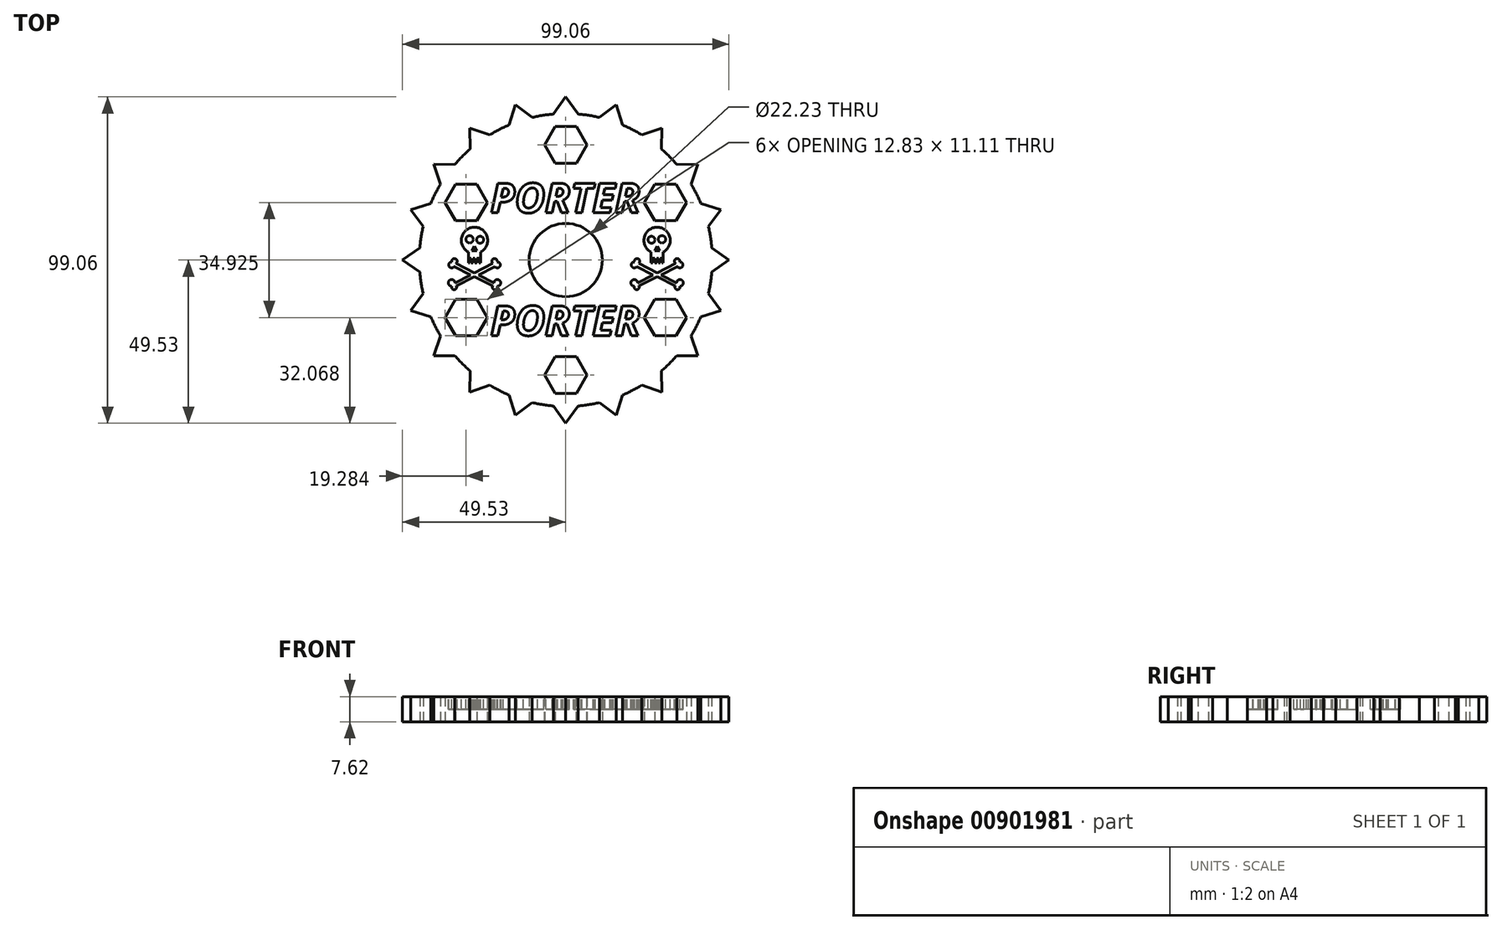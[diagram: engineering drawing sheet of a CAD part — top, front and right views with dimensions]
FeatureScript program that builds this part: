
annotation { "Feature Type Name" : "Feature", "Feature Type Description" : "" }
export const myFeature = defineFeature(function(context is Context, id is Id, definition is map)
    precondition{}
    {
        {
            var Q0;
            Q0=qCreatedBy(makeId("Top.planeOp"),FACE);
            var sketch = newSketch(context, id + "F0", { "sketchPlane" : qUnion([Q0])});
            skCircle(sketch, "E0", {"center": v(0, 0) * mm, "radius": 11.11 * mm});
            skCircle(sketch, "E1", {"center": v(0, 0) * mm, "radius": 44.45 * mm});
            skCircle(sketch, "E2.cCircle", {"center": v(0, 34.93) * mm, "radius": 5.56 * mm, "construction": true});
            skLineSegment(sketch, "E2.0", {"start": v(6.42, 34.92) * mm, "end": v(3.2, 29.37) * mm});
            skLineSegment(sketch, "E2.1", {"start": v(3.2, 29.37) * mm, "end": v(-3.2, 29.37) * mm});
            skLineSegment(sketch, "E2.2", {"start": v(-3.2, 29.37) * mm, "end": v(-6.42, 34.93) * mm});
            skLineSegment(sketch, "E2.3", {"start": v(-6.42, 34.93) * mm, "end": v(-3.2, 40.48) * mm});
            skLineSegment(sketch, "E2.4", {"start": v(-3.2, 40.48) * mm, "end": v(3.2, 40.48) * mm});
            skLineSegment(sketch, "E2.5", {"start": v(3.2, 40.48) * mm, "end": v(6.42, 34.92) * mm});
            skPoint(sketch, "E2.0.midPoint", {"position": v(4.81, 32.15) * mm});
            skCircle(sketch, "E3.1.0", {"center": v(-30.25, 17.46) * mm, "radius": 5.56 * mm, "construction": true});
            skCircle(sketch, "E3.2.0", {"center": v(-30.25, -17.46) * mm, "radius": 5.56 * mm, "construction": true});
            skCircle(sketch, "E3.3.0", {"center": v(0, -34.93) * mm, "radius": 5.56 * mm, "construction": true});
            skCircle(sketch, "E3.4.0", {"center": v(30.25, -17.46) * mm, "radius": 5.56 * mm, "construction": true});
            skCircle(sketch, "E3.5.0", {"center": v(30.25, 17.46) * mm, "radius": 5.56 * mm, "construction": true});
            skSolve(sketch);
        }
        {
            var Q0;
            Q0 = qSketchRegion(id + "F0", true);
            extrude(context, id + "F1", {"entities" : qUnion([Q0]), "depth" : 7.62 * mm, "offsetDistance" : 25.4 * mm});
        }
        {
            var Q0;
            Q0=makeQuery(id+"F1.opExtrude","CAP_FACE",FACE,{"disambiguationData":[OSD([sQuery(id+"F0.wireOp",EDGE,"E0"),sQuery(id+"F0.wireOp",EDGE,"E1"),sQuery(id+"F0.wireOp",EDGE,"E2.0"),sQuery(id+"F0.wireOp",EDGE,"E2.1"),sQuery(id+"F0.wireOp",EDGE,"E2.2"),sQuery(id+"F0.wireOp",EDGE,"E2.3"),sQuery(id+"F0.wireOp",EDGE,"E2.4"),sQuery(id+"F0.wireOp",EDGE,"E2.5")])],"isStart":true});
            var sketch = newSketch(context, id + "F2", { "sketchPlane" : qUnion([Q0])});
            skLineSegment(sketch, "E4", {"start": v(0, 0) * mm, "end": v(0, -34.93) * mm});
            skCircle(sketch, "E5.cCircle", {"center": v(0, -34.93) * mm, "radius": 5.56 * mm, "construction": true});
            skPoint(sketch, "E5.cCircle.perimeterSnap0", {"position": v(0, -40.48) * mm});
            skLineSegment(sketch, "E5.0", {"start": v(-3.2, -29.37) * mm, "end": v(3.2, -29.37) * mm});
            skLineSegment(sketch, "E5.1", {"start": v(3.2, -29.37) * mm, "end": v(6.42, -34.93) * mm});
            skLineSegment(sketch, "E5.2", {"start": v(6.42, -34.93) * mm, "end": v(3.2, -40.48) * mm});
            skLineSegment(sketch, "E5.3", {"start": v(3.2, -40.48) * mm, "end": v(-3.2, -40.48) * mm});
            skLineSegment(sketch, "E5.4", {"start": v(-3.2, -40.48) * mm, "end": v(-6.42, -34.92) * mm});
            skLineSegment(sketch, "E5.5", {"start": v(-6.42, -34.92) * mm, "end": v(-3.2, -29.37) * mm});
            skPoint(sketch, "E5.0.midPoint", {"position": v(0, -29.37) * mm});
            skPoint(sketch, "E5.0.midPoint.positionSnap0", {"position": v(0, -40.48) * mm});
            skCircle(sketch, "E6.1.0", {"center": v(30.25, -17.46) * mm, "radius": 5.56 * mm, "construction": true});
            skPoint(sketch, "E6.1.1", {"position": v(25.44, -14.68) * mm});
            skPoint(sketch, "E6.1.2", {"position": v(35.06, -20.24) * mm});
            skLineSegment(sketch, "E6.1.3", {"start": v(33.45, -23.02) * mm, "end": v(27.04, -23.02) * mm});
            skLineSegment(sketch, "E6.1.4", {"start": v(23.83, -17.46) * mm, "end": v(27.04, -11.9) * mm});
            skPoint(sketch, "E6.1.5", {"position": v(35.06, -20.24) * mm});
            skLineSegment(sketch, "E6.1.6", {"start": v(33.45, -11.9) * mm, "end": v(36.66, -17.46) * mm});
            skLineSegment(sketch, "E6.1.7", {"start": v(27.04, -23.02) * mm, "end": v(23.83, -17.46) * mm});
            skLineSegment(sketch, "E6.1.8", {"start": v(27.04, -11.9) * mm, "end": v(33.45, -11.9) * mm});
            skLineSegment(sketch, "E6.1.9", {"start": v(36.66, -17.46) * mm, "end": v(33.45, -23.02) * mm});
            skCircle(sketch, "E6.2.0", {"center": v(30.25, 17.46) * mm, "radius": 5.56 * mm, "construction": true});
            skPoint(sketch, "E6.2.1", {"position": v(25.43, 14.69) * mm});
            skPoint(sketch, "E6.2.2", {"position": v(35.06, 20.24) * mm});
            skLineSegment(sketch, "E6.2.3", {"start": v(36.66, 17.46) * mm, "end": v(33.45, 11.9) * mm});
            skLineSegment(sketch, "E6.2.4", {"start": v(27.04, 11.9) * mm, "end": v(23.83, 17.46) * mm});
            skPoint(sketch, "E6.2.5", {"position": v(35.06, 20.24) * mm});
            skLineSegment(sketch, "E6.2.6", {"start": v(27.04, 23.02) * mm, "end": v(33.45, 23.02) * mm});
            skLineSegment(sketch, "E6.2.7", {"start": v(33.45, 11.9) * mm, "end": v(27.04, 11.9) * mm});
            skLineSegment(sketch, "E6.2.8", {"start": v(23.83, 17.46) * mm, "end": v(27.04, 23.02) * mm});
            skLineSegment(sketch, "E6.2.9", {"start": v(33.45, 23.02) * mm, "end": v(36.66, 17.46) * mm});
            skCircle(sketch, "E6.3.0", {"center": v(0, 34.93) * mm, "radius": 5.56 * mm, "construction": true});
            skPoint(sketch, "E6.3.1", {"position": v(0, 29.37) * mm});
            skPoint(sketch, "E6.3.2", {"position": v(0, 40.48) * mm});
            skLineSegment(sketch, "E6.3.3", {"start": v(3.2, 40.48) * mm, "end": v(6.42, 34.92) * mm});
            skLineSegment(sketch, "E6.3.4", {"start": v(3.2, 29.37) * mm, "end": v(-3.2, 29.37) * mm});
            skPoint(sketch, "E6.3.5", {"position": v(0, 40.48) * mm});
            skLineSegment(sketch, "E6.3.6", {"start": v(-6.42, 34.93) * mm, "end": v(-3.2, 40.48) * mm});
            skLineSegment(sketch, "E6.3.7", {"start": v(6.42, 34.92) * mm, "end": v(3.2, 29.37) * mm});
            skLineSegment(sketch, "E6.3.8", {"start": v(-3.2, 29.37) * mm, "end": v(-6.42, 34.93) * mm});
            skLineSegment(sketch, "E6.3.9", {"start": v(-3.2, 40.48) * mm, "end": v(3.2, 40.48) * mm});
            skCircle(sketch, "E6.4.0", {"center": v(-30.25, 17.46) * mm, "radius": 5.56 * mm, "construction": true});
            skPoint(sketch, "E6.4.1", {"position": v(-25.44, 14.68) * mm});
            skPoint(sketch, "E6.4.2", {"position": v(-35.06, 20.24) * mm});
            skLineSegment(sketch, "E6.4.3", {"start": v(-33.45, 23.02) * mm, "end": v(-27.04, 23.02) * mm});
            skLineSegment(sketch, "E6.4.4", {"start": v(-23.83, 17.46) * mm, "end": v(-27.04, 11.9) * mm});
            skPoint(sketch, "E6.4.5", {"position": v(-35.06, 20.24) * mm});
            skLineSegment(sketch, "E6.4.6", {"start": v(-33.45, 11.9) * mm, "end": v(-36.66, 17.46) * mm});
            skLineSegment(sketch, "E6.4.7", {"start": v(-27.04, 23.02) * mm, "end": v(-23.83, 17.46) * mm});
            skLineSegment(sketch, "E6.4.8", {"start": v(-27.04, 11.9) * mm, "end": v(-33.45, 11.9) * mm});
            skLineSegment(sketch, "E6.4.9", {"start": v(-36.66, 17.46) * mm, "end": v(-33.45, 23.02) * mm});
            skCircle(sketch, "E6.5.0", {"center": v(-30.25, -17.46) * mm, "radius": 5.56 * mm, "construction": true});
            skPoint(sketch, "E6.5.1", {"position": v(-25.43, -14.69) * mm});
            skPoint(sketch, "E6.5.2", {"position": v(-35.06, -20.24) * mm});
            skLineSegment(sketch, "E6.5.3", {"start": v(-36.66, -17.46) * mm, "end": v(-33.45, -11.9) * mm});
            skLineSegment(sketch, "E6.5.4", {"start": v(-27.04, -11.9) * mm, "end": v(-23.83, -17.46) * mm});
            skPoint(sketch, "E6.5.5", {"position": v(-35.06, -20.24) * mm});
            skLineSegment(sketch, "E6.5.6", {"start": v(-27.04, -23.02) * mm, "end": v(-33.45, -23.02) * mm});
            skLineSegment(sketch, "E6.5.7", {"start": v(-33.45, -11.9) * mm, "end": v(-27.04, -11.9) * mm});
            skLineSegment(sketch, "E6.5.8", {"start": v(-23.83, -17.46) * mm, "end": v(-27.04, -23.02) * mm});
            skLineSegment(sketch, "E6.5.9", {"start": v(-33.45, -23.02) * mm, "end": v(-36.66, -17.46) * mm});
            skPoint(sketch, "E6.center", {"position": v(0, 0) * mm});
            skSolve(sketch);
        }
        {
            var Q0;
            Q0 = qSketchRegion(id + "F2", true);
            extrude(context, id + "F3", {"entities" : qUnion([Q0]), "operationType" : NewBodyOperationType.REMOVE, "oppositeDirection" : true, "depth" : 25.4 * mm, "offsetDistance" : 25.4 * mm});
        }
        {
            var Q0;
            Q0=makeQuery(id+"F1.opExtrude","CAP_FACE",FACE,{"disambiguationData":[OSD([sQuery(id+"F0.wireOp",EDGE,"E0"),sQuery(id+"F0.wireOp",EDGE,"E1"),sQuery(id+"F0.wireOp",EDGE,"E2.0"),sQuery(id+"F0.wireOp",EDGE,"E2.1"),sQuery(id+"F0.wireOp",EDGE,"E2.2"),sQuery(id+"F0.wireOp",EDGE,"E2.3"),sQuery(id+"F0.wireOp",EDGE,"E2.4"),sQuery(id+"F0.wireOp",EDGE,"E2.5")])],"isStart":false});
            var sketch = newSketch(context, id + "F4", { "sketchPlane" : qUnion([Q0])});
            skText(sketch, "E7", { "text": "PORTER", "fontName": "OpenSans-BoldItalic.ttf"});
            skText(sketch, "E8", { "text": "PORTER", "fontName": "OpenSans-BoldItalic.ttf"});
            const initialGuessF4  = {"E7": [-0.0228, -0.02292, 1, 0, 0.00907], "E8": [-0.0228, 0.01432, 1, 0, 0.00907]};
            skSetInitialGuess(sketch, initialGuessF4);
            skSolve(sketch);
        }
        {
            var Q0;
            Q0 = qSketchRegion(id + "F4", true);
            extrude(context, id + "F5", {"entities" : qUnion([Q0]), "operationType" : NewBodyOperationType.REMOVE, "oppositeDirection" : true, "depth" : 3.8 * mm, "offsetDistance" : 25.4 * mm});
        }
        {
            var Q0;
            {var subQ0=sQuery(id+"F0.wireOp",EDGE,"E2.5");var subQ1=sQuery(id+"F0.wireOp",EDGE,"E2.4");var subQ2=sQuery(id+"F0.wireOp",EDGE,"E2.0");var subQ3=sQuery(id+"F0.wireOp",EDGE,"E1");var subQ4=sQuery(id+"F0.wireOp",EDGE,"E2.1");var subQ5=sQuery(id+"F0.wireOp",EDGE,"E2.2");var subQ6=sQuery(id+"F0.wireOp",EDGE,"E0");var subQ7=sQuery(id+"F0.wireOp",EDGE,"E2.3");Q0=makeQuery(id+"F5.boolean.opBoolean","SPLIT",FACE,{"disambiguationData":[TD([makeQuery(id+"F1.opExtrude","SWEPT_FACE",FACE,{"disambiguationData":[OSD([subQ6])]})])],"derivedFrom":makeQuery(id+"F1.opExtrude","CAP_FACE",FACE,{"disambiguationData":[OSD([subQ6,subQ3,subQ2,subQ4,subQ5,subQ7,subQ1,subQ0])],"isStart":false})});}
            var sketch = newSketch(context, id + "F6", { "sketchPlane" : qUnion([Q0])});
            skLineSegment(sketch, "E9", {"start": v(0, 49.53) * mm, "end": v(4.7, 42.86) * mm});
            skLineSegment(sketch, "E10.MirrorCS", {"start": v(0, 49.53) * mm, "end": v(-4.7, 42.86) * mm});
            skLineSegment(sketch, "E11", {"start": v(-4.7, 42.86) * mm, "end": v(4.7, 42.86) * mm});
            skLineSegment(sketch, "E12.1.0", {"start": v(-15.3, 47.1) * mm, "end": v(-8.77, 42.22) * mm});
            skLineSegment(sketch, "E12.1.1", {"start": v(-17.72, 39.3) * mm, "end": v(-8.77, 42.22) * mm});
            skLineSegment(sketch, "E12.1.2", {"start": v(-15.3, 47.1) * mm, "end": v(-17.72, 39.3) * mm});
            skLineSegment(sketch, "E12.2.0", {"start": v(-29.11, 40.07) * mm, "end": v(-21.38, 37.44) * mm});
            skLineSegment(sketch, "E12.2.1", {"start": v(-29, 31.9) * mm, "end": v(-21.38, 37.44) * mm});
            skLineSegment(sketch, "E12.2.2", {"start": v(-29.11, 40.07) * mm, "end": v(-29, 31.9) * mm});
            skLineSegment(sketch, "E12.3.0", {"start": v(-40.07, 29.11) * mm, "end": v(-31.9, 29) * mm});
            skLineSegment(sketch, "E12.3.1", {"start": v(-37.44, 21.38) * mm, "end": v(-31.9, 29) * mm});
            skLineSegment(sketch, "E12.3.2", {"start": v(-40.07, 29.11) * mm, "end": v(-37.44, 21.38) * mm});
            skLineSegment(sketch, "E12.4.0", {"start": v(-47.1, 15.3) * mm, "end": v(-39.3, 17.72) * mm});
            skLineSegment(sketch, "E12.4.1", {"start": v(-42.22, 8.77) * mm, "end": v(-39.3, 17.72) * mm});
            skLineSegment(sketch, "E12.4.2", {"start": v(-47.1, 15.3) * mm, "end": v(-42.22, 8.77) * mm});
            skLineSegment(sketch, "E12.5.0", {"start": v(-49.53, 0) * mm, "end": v(-42.86, 4.7) * mm});
            skLineSegment(sketch, "E12.5.1", {"start": v(-42.86, -4.7) * mm, "end": v(-42.86, 4.7) * mm});
            skLineSegment(sketch, "E12.5.2", {"start": v(-49.53, 0) * mm, "end": v(-42.86, -4.7) * mm});
            skLineSegment(sketch, "E12.6.0", {"start": v(-47.1, -15.3) * mm, "end": v(-42.22, -8.77) * mm});
            skLineSegment(sketch, "E12.6.1", {"start": v(-39.3, -17.72) * mm, "end": v(-42.22, -8.77) * mm});
            skLineSegment(sketch, "E12.6.2", {"start": v(-47.1, -15.3) * mm, "end": v(-39.3, -17.72) * mm});
            skLineSegment(sketch, "E12.7.0", {"start": v(-40.07, -29.11) * mm, "end": v(-37.44, -21.38) * mm});
            skLineSegment(sketch, "E12.7.1", {"start": v(-31.9, -29) * mm, "end": v(-37.44, -21.38) * mm});
            skLineSegment(sketch, "E12.7.2", {"start": v(-40.07, -29.11) * mm, "end": v(-31.9, -29) * mm});
            skLineSegment(sketch, "E12.8.0", {"start": v(-29.11, -40.07) * mm, "end": v(-29, -31.9) * mm});
            skLineSegment(sketch, "E12.8.1", {"start": v(-21.38, -37.44) * mm, "end": v(-29, -31.9) * mm});
            skLineSegment(sketch, "E12.8.2", {"start": v(-29.11, -40.07) * mm, "end": v(-21.38, -37.44) * mm});
            skLineSegment(sketch, "E12.9.0", {"start": v(-15.3, -47.1) * mm, "end": v(-17.72, -39.3) * mm});
            skLineSegment(sketch, "E12.9.1", {"start": v(-8.77, -42.22) * mm, "end": v(-17.72, -39.3) * mm});
            skLineSegment(sketch, "E12.9.2", {"start": v(-15.3, -47.1) * mm, "end": v(-8.77, -42.22) * mm});
            skLineSegment(sketch, "E12.10.0", {"start": v(0, -49.53) * mm, "end": v(-4.7, -42.86) * mm});
            skLineSegment(sketch, "E12.10.1", {"start": v(4.7, -42.86) * mm, "end": v(-4.7, -42.86) * mm});
            skLineSegment(sketch, "E12.10.2", {"start": v(0, -49.53) * mm, "end": v(4.7, -42.86) * mm});
            skLineSegment(sketch, "E12.11.0", {"start": v(15.3, -47.1) * mm, "end": v(8.77, -42.22) * mm});
            skLineSegment(sketch, "E12.11.1", {"start": v(17.72, -39.3) * mm, "end": v(8.77, -42.22) * mm});
            skLineSegment(sketch, "E12.11.2", {"start": v(15.3, -47.1) * mm, "end": v(17.72, -39.3) * mm});
            skLineSegment(sketch, "E12.12.0", {"start": v(29.11, -40.07) * mm, "end": v(21.38, -37.44) * mm});
            skLineSegment(sketch, "E12.12.1", {"start": v(29, -31.9) * mm, "end": v(21.38, -37.44) * mm});
            skLineSegment(sketch, "E12.12.2", {"start": v(29.11, -40.07) * mm, "end": v(29, -31.9) * mm});
            skLineSegment(sketch, "E12.13.0", {"start": v(40.07, -29.11) * mm, "end": v(31.9, -29) * mm});
            skLineSegment(sketch, "E12.13.1", {"start": v(37.44, -21.38) * mm, "end": v(31.9, -29) * mm});
            skLineSegment(sketch, "E12.13.2", {"start": v(40.07, -29.11) * mm, "end": v(37.44, -21.38) * mm});
            skLineSegment(sketch, "E12.14.0", {"start": v(47.1, -15.3) * mm, "end": v(39.3, -17.72) * mm});
            skLineSegment(sketch, "E12.14.1", {"start": v(42.22, -8.77) * mm, "end": v(39.3, -17.72) * mm});
            skLineSegment(sketch, "E12.14.2", {"start": v(47.1, -15.3) * mm, "end": v(42.22, -8.77) * mm});
            skLineSegment(sketch, "E12.15.0", {"start": v(49.53, 0) * mm, "end": v(42.86, -4.7) * mm});
            skLineSegment(sketch, "E12.15.1", {"start": v(42.86, 4.7) * mm, "end": v(42.86, -4.7) * mm});
            skLineSegment(sketch, "E12.15.2", {"start": v(49.53, 0) * mm, "end": v(42.86, 4.7) * mm});
            skLineSegment(sketch, "E12.16.0", {"start": v(47.1, 15.3) * mm, "end": v(42.22, 8.77) * mm});
            skLineSegment(sketch, "E12.16.1", {"start": v(39.3, 17.72) * mm, "end": v(42.22, 8.77) * mm});
            skLineSegment(sketch, "E12.16.2", {"start": v(47.1, 15.3) * mm, "end": v(39.3, 17.72) * mm});
            skLineSegment(sketch, "E12.17.0", {"start": v(40.07, 29.11) * mm, "end": v(37.44, 21.38) * mm});
            skLineSegment(sketch, "E12.17.1", {"start": v(31.9, 29) * mm, "end": v(37.44, 21.38) * mm});
            skLineSegment(sketch, "E12.17.2", {"start": v(40.07, 29.11) * mm, "end": v(31.9, 29) * mm});
            skLineSegment(sketch, "E12.18.0", {"start": v(29.11, 40.07) * mm, "end": v(29, 31.9) * mm});
            skLineSegment(sketch, "E12.18.1", {"start": v(21.38, 37.44) * mm, "end": v(29, 31.9) * mm});
            skLineSegment(sketch, "E12.18.2", {"start": v(29.11, 40.07) * mm, "end": v(21.38, 37.44) * mm});
            skLineSegment(sketch, "E12.19.0", {"start": v(15.3, 47.1) * mm, "end": v(17.72, 39.3) * mm});
            skLineSegment(sketch, "E12.19.1", {"start": v(8.77, 42.22) * mm, "end": v(17.72, 39.3) * mm});
            skLineSegment(sketch, "E12.19.2", {"start": v(15.3, 47.1) * mm, "end": v(8.77, 42.22) * mm});
            skPoint(sketch, "E12.center", {"position": v(0, 0) * mm});
            skSolve(sketch);
        }
        {
            var Q0;
            Q0 = qSketchRegion(id + "F6", true);
            extrude(context, id + "F7", {"entities" : qUnion([Q0]), "operationType" : NewBodyOperationType.ADD, "oppositeDirection" : true, "depth" : 7.62 * mm, "offsetDistance" : 25.4 * mm});
        }
        {
            var Q0;
            {var subQ0=sQuery(id+"F0.wireOp",EDGE,"E2.5");var subQ1=sQuery(id+"F0.wireOp",EDGE,"E2.4");var subQ2=sQuery(id+"F0.wireOp",EDGE,"E2.0");var subQ3=sQuery(id+"F0.wireOp",EDGE,"E1");var subQ4=sQuery(id+"F0.wireOp",EDGE,"E2.1");var subQ5=sQuery(id+"F0.wireOp",EDGE,"E2.2");var subQ6=sQuery(id+"F0.wireOp",EDGE,"E0");var subQ7=sQuery(id+"F0.wireOp",EDGE,"E2.3");Q0=makeQuery(id+"F7.boolean.opBoolean","MERGE",FACE,{"derivedFrom":[makeQuery(id+"F5.boolean.opBoolean","SPLIT",FACE,{"disambiguationData":[TD([makeQuery(id+"F1.opExtrude","SWEPT_FACE",FACE,{"disambiguationData":[OSD([subQ6])]})])],"derivedFrom":makeQuery(id+"F1.opExtrude","CAP_FACE",FACE,{"disambiguationData":[OSD([subQ6,subQ3,subQ2,subQ4,subQ5,subQ7,subQ1,subQ0])],"isStart":false})}),makeQuery(id+"F7.opExtrude","CAP_FACE",FACE,{"disambiguationData":[OSD([sQuery(id+"F6.wireOp",EDGE,"E9"),sQuery(id+"F6.wireOp",EDGE,"E10.MirrorCS"),sQuery(id+"F6.wireOp",EDGE,"E11")])],"isStart":true}),makeQuery(id+"F7.opExtrude","CAP_FACE",FACE,{"disambiguationData":[OSD([sQuery(id+"F6.wireOp",EDGE,"E12.1.0"),sQuery(id+"F6.wireOp",EDGE,"E12.1.1"),sQuery(id+"F6.wireOp",EDGE,"E12.1.2")])],"isStart":true}),makeQuery(id+"F7.opExtrude","CAP_FACE",FACE,{"disambiguationData":[OSD([sQuery(id+"F6.wireOp",EDGE,"E12.2.0"),sQuery(id+"F6.wireOp",EDGE,"E12.2.1"),sQuery(id+"F6.wireOp",EDGE,"E12.2.2")])],"isStart":true}),makeQuery(id+"F7.opExtrude","CAP_FACE",FACE,{"disambiguationData":[OSD([sQuery(id+"F6.wireOp",EDGE,"E12.3.0"),sQuery(id+"F6.wireOp",EDGE,"E12.3.1"),sQuery(id+"F6.wireOp",EDGE,"E12.3.2")])],"isStart":true}),makeQuery(id+"F7.opExtrude","CAP_FACE",FACE,{"disambiguationData":[OSD([sQuery(id+"F6.wireOp",EDGE,"E12.4.0"),sQuery(id+"F6.wireOp",EDGE,"E12.4.1"),sQuery(id+"F6.wireOp",EDGE,"E12.4.2")])],"isStart":true}),makeQuery(id+"F7.opExtrude","CAP_FACE",FACE,{"disambiguationData":[OSD([sQuery(id+"F6.wireOp",EDGE,"E12.5.0"),sQuery(id+"F6.wireOp",EDGE,"E12.5.1"),sQuery(id+"F6.wireOp",EDGE,"E12.5.2")])],"isStart":true}),makeQuery(id+"F7.opExtrude","CAP_FACE",FACE,{"disambiguationData":[OSD([sQuery(id+"F6.wireOp",EDGE,"E12.6.0"),sQuery(id+"F6.wireOp",EDGE,"E12.6.1"),sQuery(id+"F6.wireOp",EDGE,"E12.6.2")])],"isStart":true}),makeQuery(id+"F7.opExtrude","CAP_FACE",FACE,{"disambiguationData":[OSD([sQuery(id+"F6.wireOp",EDGE,"E12.7.0"),sQuery(id+"F6.wireOp",EDGE,"E12.7.1"),sQuery(id+"F6.wireOp",EDGE,"E12.7.2")])],"isStart":true}),makeQuery(id+"F7.opExtrude","CAP_FACE",FACE,{"disambiguationData":[OSD([sQuery(id+"F6.wireOp",EDGE,"E12.8.0"),sQuery(id+"F6.wireOp",EDGE,"E12.8.1"),sQuery(id+"F6.wireOp",EDGE,"E12.8.2")])],"isStart":true}),makeQuery(id+"F7.opExtrude","CAP_FACE",FACE,{"disambiguationData":[OSD([sQuery(id+"F6.wireOp",EDGE,"E12.9.0"),sQuery(id+"F6.wireOp",EDGE,"E12.9.1"),sQuery(id+"F6.wireOp",EDGE,"E12.9.2")])],"isStart":true}),makeQuery(id+"F7.opExtrude","CAP_FACE",FACE,{"disambiguationData":[OSD([sQuery(id+"F6.wireOp",EDGE,"E12.10.0"),sQuery(id+"F6.wireOp",EDGE,"E12.10.1"),sQuery(id+"F6.wireOp",EDGE,"E12.10.2")])],"isStart":true}),makeQuery(id+"F7.opExtrude","CAP_FACE",FACE,{"disambiguationData":[OSD([sQuery(id+"F6.wireOp",EDGE,"E12.11.0"),sQuery(id+"F6.wireOp",EDGE,"E12.11.1"),sQuery(id+"F6.wireOp",EDGE,"E12.11.2")])],"isStart":true}),makeQuery(id+"F7.opExtrude","CAP_FACE",FACE,{"disambiguationData":[OSD([sQuery(id+"F6.wireOp",EDGE,"E12.12.0"),sQuery(id+"F6.wireOp",EDGE,"E12.12.1"),sQuery(id+"F6.wireOp",EDGE,"E12.12.2")])],"isStart":true}),makeQuery(id+"F7.opExtrude","CAP_FACE",FACE,{"disambiguationData":[OSD([sQuery(id+"F6.wireOp",EDGE,"E12.13.0"),sQuery(id+"F6.wireOp",EDGE,"E12.13.1"),sQuery(id+"F6.wireOp",EDGE,"E12.13.2")])],"isStart":true}),makeQuery(id+"F7.opExtrude","CAP_FACE",FACE,{"disambiguationData":[OSD([sQuery(id+"F6.wireOp",EDGE,"E12.14.0"),sQuery(id+"F6.wireOp",EDGE,"E12.14.1"),sQuery(id+"F6.wireOp",EDGE,"E12.14.2")])],"isStart":true}),makeQuery(id+"F7.opExtrude","CAP_FACE",FACE,{"disambiguationData":[OSD([sQuery(id+"F6.wireOp",EDGE,"E12.15.0"),sQuery(id+"F6.wireOp",EDGE,"E12.15.1"),sQuery(id+"F6.wireOp",EDGE,"E12.15.2")])],"isStart":true}),makeQuery(id+"F7.opExtrude","CAP_FACE",FACE,{"disambiguationData":[OSD([sQuery(id+"F6.wireOp",EDGE,"E12.16.0"),sQuery(id+"F6.wireOp",EDGE,"E12.16.1"),sQuery(id+"F6.wireOp",EDGE,"E12.16.2")])],"isStart":true}),makeQuery(id+"F7.opExtrude","CAP_FACE",FACE,{"disambiguationData":[OSD([sQuery(id+"F6.wireOp",EDGE,"E12.17.0"),sQuery(id+"F6.wireOp",EDGE,"E12.17.1"),sQuery(id+"F6.wireOp",EDGE,"E12.17.2")])],"isStart":true}),makeQuery(id+"F7.opExtrude","CAP_FACE",FACE,{"disambiguationData":[OSD([sQuery(id+"F6.wireOp",EDGE,"E12.18.0"),sQuery(id+"F6.wireOp",EDGE,"E12.18.1"),sQuery(id+"F6.wireOp",EDGE,"E12.18.2")])],"isStart":true}),makeQuery(id+"F7.opExtrude","CAP_FACE",FACE,{"disambiguationData":[OSD([sQuery(id+"F6.wireOp",EDGE,"E12.19.0"),sQuery(id+"F6.wireOp",EDGE,"E12.19.1"),sQuery(id+"F6.wireOp",EDGE,"E12.19.2")])],"isStart":true})]});}
            var sketch = newSketch(context, id + "F8", { "sketchPlane" : qUnion([Q0])});
            skArc(sketch, "E13", {"start": v(29.58, 2.43) * mm, "mid": v(27.7, 9.97) * mm, "end": v(25.83, 2.43) * mm});
            skLineSegment(sketch, "E14.left", {"start": v(29.58, 2.43) * mm, "end": v(29.58, -0.87) * mm});
            skLineSegment(sketch, "E14.right", {"start": v(25.83, 2.43) * mm, "end": v(25.83, -0.87) * mm});
            skPoint(sketch, "E14.middle", {"position": v(27.7, 0.58) * mm});
            skLineSegment(sketch, "E15", {"start": v(25.83, -0.87) * mm, "end": v(26.37, -0.87) * mm});
            skLineSegment(sketch, "E16.top", {"start": v(26.37, 0.57) * mm, "end": v(26.97, 0.57) * mm});
            skLineSegment(sketch, "E16.left", {"start": v(26.37, -0.87) * mm, "end": v(26.37, 0.57) * mm});
            skLineSegment(sketch, "E16.right", {"start": v(26.97, -0.87) * mm, "end": v(26.97, 0.57) * mm});
            skLineSegment(sketch, "E17.top", {"start": v(27.58, 0.5) * mm, "end": v(28.12, 0.5) * mm});
            skLineSegment(sketch, "E17.left", {"start": v(27.58, -0.87) * mm, "end": v(27.58, 0.5) * mm});
            skLineSegment(sketch, "E17.right", {"start": v(28.12, -0.87) * mm, "end": v(28.12, 0.5) * mm});
            skLineSegment(sketch, "E18.top", {"start": v(28.7, 0.54) * mm, "end": v(29.18, 0.54) * mm});
            skLineSegment(sketch, "E18.left", {"start": v(28.7, -0.87) * mm, "end": v(28.7, 0.54) * mm});
            skLineSegment(sketch, "E18.right", {"start": v(29.18, -0.87) * mm, "end": v(29.18, 0.54) * mm});
            skLineSegment(sketch, "E19.trimOffspring", {"start": v(26.97, -0.87) * mm, "end": v(27.58, -0.87) * mm});
            skLineSegment(sketch, "E20.trimOffspring", {"start": v(28.12, -0.87) * mm, "end": v(28.7, -0.87) * mm});
            skLineSegment(sketch, "E21.trimOffspring", {"start": v(29.18, -0.87) * mm, "end": v(29.58, -0.87) * mm});
            skCircle(sketch, "E22", {"center": v(26, 6.15) * mm, "radius": 1.05 * mm});
            skCircle(sketch, "E23", {"center": v(29.19, 6.28) * mm, "radius": 1.12 * mm});
            skLineSegment(sketch, "E24", {"start": v(27.73, 4.24) * mm, "end": v(27.01, 2.87) * mm});
            skLineSegment(sketch, "E25", {"start": v(27.01, 2.87) * mm, "end": v(28.51, 2.87) * mm});
            skLineSegment(sketch, "E26", {"start": v(28.51, 2.87) * mm, "end": v(27.73, 4.24) * mm});
            skArc(sketch, "E27", {"start": v(22.12, -1) * mm, "mid": v(21.88, 0.4) * mm, "end": v(20.84, -0.57) * mm});
            skArc(sketch, "E28", {"start": v(20.84, -0.57) * mm, "mid": v(19.96, -1.89) * mm, "end": v(21.54, -1.99) * mm});
            skLineSegment(sketch, "E29", {"start": v(22.12, -1) * mm, "end": v(27.7, -3.89) * mm});
            skLineSegment(sketch, "E30", {"start": v(21.54, -1.99) * mm, "end": v(26.5, -4.5) * mm});
            skArc(sketch, "E31", {"start": v(33.21, -7.9) * mm, "mid": v(33.86, -9) * mm, "end": v(34.57, -7.96) * mm});
            skArc(sketch, "E32", {"start": v(34.57, -7.96) * mm, "mid": v(35.38, -6.26) * mm, "end": v(33.63, -6.95) * mm});
            skArc(sketch, "E33.MirrorCS", {"start": v(20.84, -7.96) * mm, "mid": v(20.03, -6.26) * mm, "end": v(21.78, -6.95) * mm});
            skArc(sketch, "E34.MirrorCS", {"start": v(22.2, -7.9) * mm, "mid": v(21.55, -9) * mm, "end": v(20.84, -7.96) * mm});
            skLineSegment(sketch, "E35.MirrorCS", {"start": v(33.87, -1.99) * mm, "end": v(28.9, -4.5) * mm});
            skLineSegment(sketch, "E36.MirrorCS", {"start": v(33.29, -1) * mm, "end": v(27.7, -3.89) * mm});
            skArc(sketch, "E37.MirrorCS", {"start": v(33.29, -1) * mm, "mid": v(33.53, 0.4) * mm, "end": v(34.57, -0.57) * mm});
            skArc(sketch, "E38.MirrorCS", {"start": v(34.57, -0.57) * mm, "mid": v(35.44, -1.89) * mm, "end": v(33.87, -1.99) * mm});
            skLineSegment(sketch, "E39.trimOffspring", {"start": v(26.5, -4.5) * mm, "end": v(21.78, -6.95) * mm});
            skLineSegment(sketch, "E40.trimOffspring", {"start": v(28.9, -4.5) * mm, "end": v(33.63, -6.95) * mm});
            skLineSegment(sketch, "E41.trimOffspring", {"start": v(27.7, -5.12) * mm, "end": v(22.2, -7.9) * mm});
            skLineSegment(sketch, "E42.trimOffspring", {"start": v(27.7, -5.12) * mm, "end": v(33.21, -7.9) * mm});
            skPoint(sketch, "E43.end.orphan", {"position": v(27.7, 1.1) * mm});
            skPoint(sketch, "E43.start.orphan", {"position": v(27.7, 2.16) * mm});
            skLineSegment(sketch, "E44.MirrorCS", {"start": v(-28.7, 0.54) * mm, "end": v(-29.18, 0.54) * mm});
            skLineSegment(sketch, "E45.MirrorCS", {"start": v(-29.18, -0.87) * mm, "end": v(-29.58, -0.87) * mm});
            skLineSegment(sketch, "E46.MirrorCS", {"start": v(-27.58, 0.5) * mm, "end": v(-28.12, 0.5) * mm});
            skLineSegment(sketch, "E47.MirrorCS", {"start": v(-28.12, -0.87) * mm, "end": v(-28.12, 0.5) * mm});
            skLineSegment(sketch, "E48.MirrorCS", {"start": v(-26.97, -0.87) * mm, "end": v(-27.58, -0.87) * mm});
            skLineSegment(sketch, "E49.MirrorCS", {"start": v(-28.7, -0.87) * mm, "end": v(-28.7, 0.54) * mm});
            skLineSegment(sketch, "E50.MirrorCS", {"start": v(-27.58, -0.87) * mm, "end": v(-27.58, 0.5) * mm});
            skLineSegment(sketch, "E51.MirrorCS", {"start": v(-29.18, -0.87) * mm, "end": v(-29.18, 0.54) * mm});
            skLineSegment(sketch, "E52.MirrorCS", {"start": v(-28.12, -0.87) * mm, "end": v(-28.7, -0.87) * mm});
            skLineSegment(sketch, "E53.MirrorCS", {"start": v(-26.97, -0.87) * mm, "end": v(-26.97, 0.57) * mm});
            skLineSegment(sketch, "E54.MirrorCS", {"start": v(-26.37, 0.57) * mm, "end": v(-26.97, 0.57) * mm});
            skLineSegment(sketch, "E55.MirrorCS", {"start": v(-25.83, 2.43) * mm, "end": v(-25.83, -0.87) * mm});
            skLineSegment(sketch, "E56.MirrorCS", {"start": v(-25.83, -0.87) * mm, "end": v(-26.37, -0.87) * mm});
            skLineSegment(sketch, "E57.MirrorCS", {"start": v(-28.51, 2.87) * mm, "end": v(-27.73, 4.24) * mm});
            skArc(sketch, "E58.MirrorCS", {"start": v(-22.12, -1) * mm, "mid": v(-21.88, 0.4) * mm, "end": v(-20.84, -0.57) * mm});
            skLineSegment(sketch, "E59.MirrorCS", {"start": v(-29.58, 2.43) * mm, "end": v(-29.58, -0.87) * mm});
            skLineSegment(sketch, "E60.MirrorCS", {"start": v(-27.73, 4.24) * mm, "end": v(-27.01, 2.87) * mm});
            skLineSegment(sketch, "E61.MirrorCS", {"start": v(-26.37, -0.87) * mm, "end": v(-26.37, 0.57) * mm});
            skLineSegment(sketch, "E62.MirrorCS", {"start": v(-27.01, 2.87) * mm, "end": v(-28.51, 2.87) * mm});
            skArc(sketch, "E63.MirrorCS", {"start": v(-22.2, -7.9) * mm, "mid": v(-21.55, -9) * mm, "end": v(-20.84, -7.96) * mm});
            skLineSegment(sketch, "E64.MirrorCS", {"start": v(-33.29, -1) * mm, "end": v(-27.7, -3.89) * mm});
            skArc(sketch, "E65.MirrorCS", {"start": v(-34.57, -0.57) * mm, "mid": v(-35.44, -1.89) * mm, "end": v(-33.87, -1.99) * mm});
            skArc(sketch, "E66.MirrorCS", {"start": v(-20.84, -0.57) * mm, "mid": v(-19.96, -1.89) * mm, "end": v(-21.54, -1.99) * mm});
            skLineSegment(sketch, "E67.MirrorCS", {"start": v(-26.5, -4.5) * mm, "end": v(-21.78, -6.95) * mm});
            skLineSegment(sketch, "E68.MirrorCS", {"start": v(-27.7, -5.12) * mm, "end": v(-22.2, -7.9) * mm});
            skArc(sketch, "E69.MirrorCS", {"start": v(-34.57, -7.96) * mm, "mid": v(-35.38, -6.26) * mm, "end": v(-33.63, -6.95) * mm});
            skArc(sketch, "E70.MirrorCS", {"start": v(-33.21, -7.9) * mm, "mid": v(-33.86, -9) * mm, "end": v(-34.57, -7.96) * mm});
            skLineSegment(sketch, "E71.MirrorCS", {"start": v(-33.87, -1.99) * mm, "end": v(-28.9, -4.5) * mm});
            skArc(sketch, "E72.MirrorCS", {"start": v(-33.29, -1) * mm, "mid": v(-33.53, 0.4) * mm, "end": v(-34.57, -0.57) * mm});
            skArc(sketch, "E73.MirrorCS", {"start": v(-20.84, -7.96) * mm, "mid": v(-20.03, -6.26) * mm, "end": v(-21.78, -6.95) * mm});
            skLineSegment(sketch, "E74.MirrorCS", {"start": v(-21.54, -1.99) * mm, "end": v(-26.5, -4.5) * mm});
            skLineSegment(sketch, "E75.MirrorCS", {"start": v(-28.9, -4.5) * mm, "end": v(-33.63, -6.95) * mm});
            skPoint(sketch, "E76.MirrorP", {"position": v(-27.7, 1.1) * mm});
            skLineSegment(sketch, "E77.MirrorCS", {"start": v(-22.12, -1) * mm, "end": v(-27.7, -3.89) * mm});
            skLineSegment(sketch, "E78.MirrorCS", {"start": v(-27.7, -5.12) * mm, "end": v(-33.21, -7.9) * mm});
            skPoint(sketch, "E79.MirrorP", {"position": v(-27.7, 2.16) * mm});
            skPoint(sketch, "E80.MirrorP", {"position": v(-27.7, 0.58) * mm});
            skCircle(sketch, "E81.MirrorC", {"center": v(-26, 6.15) * mm, "radius": 1.05 * mm});
            skCircle(sketch, "E82.MirrorC", {"center": v(-29.19, 6.28) * mm, "radius": 1.12 * mm});
            skArc(sketch, "E83.MirrorCS", {"start": v(-29.58, 2.43) * mm, "mid": v(-27.7, 9.97) * mm, "end": v(-25.83, 2.43) * mm});
            skSolve(sketch);
        }
        {
            var Q0;
            Q0 = qSketchRegion(id + "F8", true);
            extrude(context, id + "F9", {"entities" : qUnion([Q0]), "operationType" : NewBodyOperationType.REMOVE, "oppositeDirection" : true, "depth" : 3.8 * mm, "offsetDistance" : 25.4 * mm});
        }
    });
